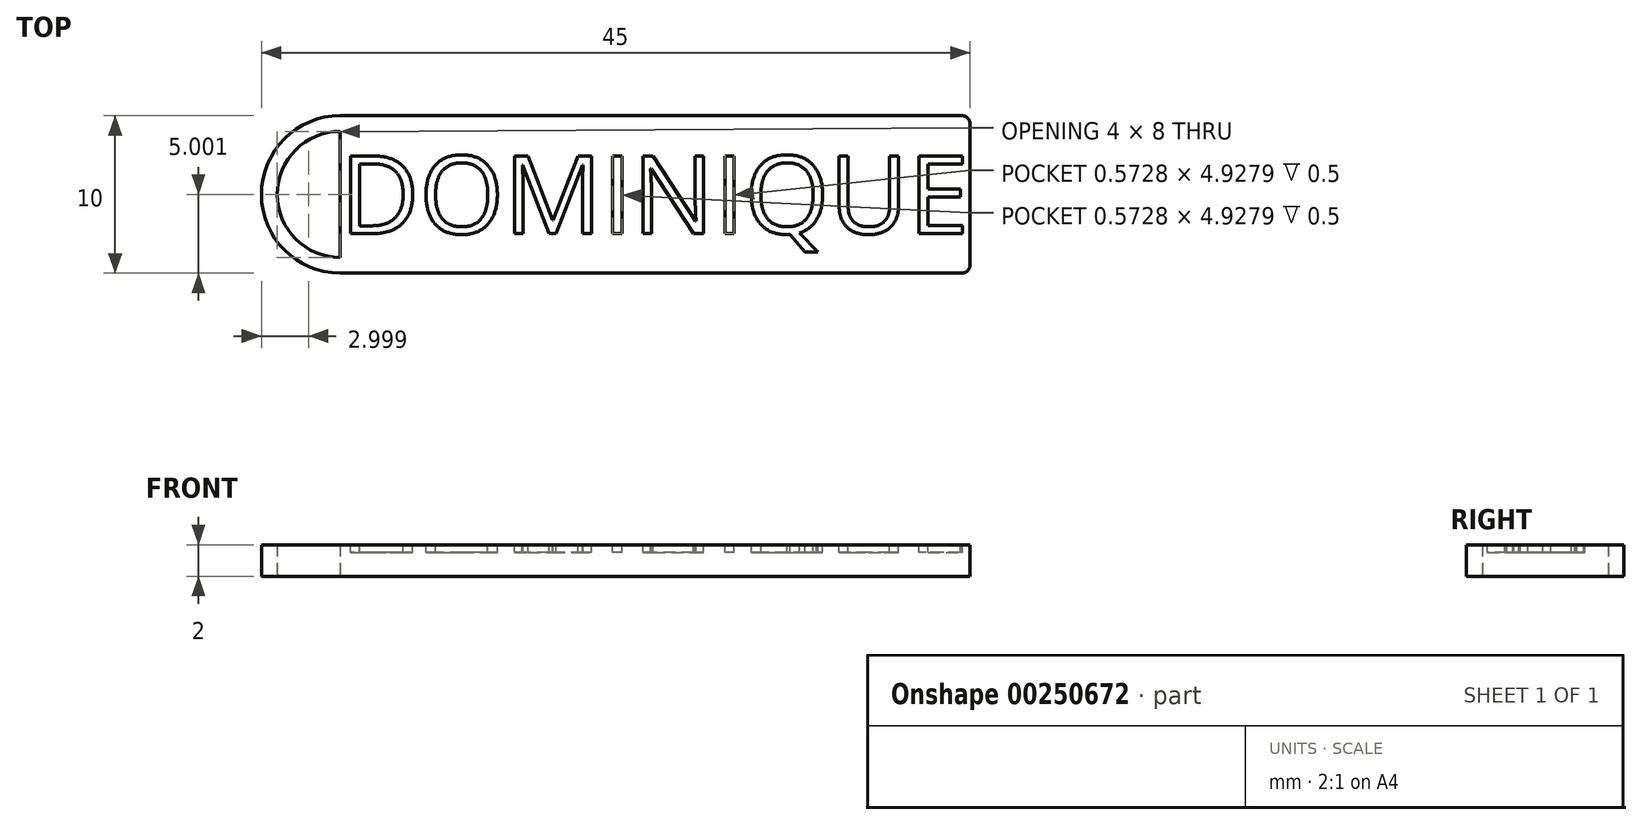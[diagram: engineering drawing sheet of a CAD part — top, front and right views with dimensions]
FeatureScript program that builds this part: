
annotation { "Feature Type Name" : "Feature", "Feature Type Description" : "" }
export const myFeature = defineFeature(function(context is Context, id is Id, definition is map)
    precondition{}
    {
        {
            var Q0;
            Q0=qCreatedBy(makeId("Top.planeOp"),FACE);
            var sketch = newSketch(context, id + "F0", { "sketchPlane" : qUnion([Q0])});
            skLineSegment(sketch, "E0.bottom", {"start": v(-5.27, 3.22) * mm, "end": v(34.73, 3.22) * mm});
            skLineSegment(sketch, "E0.top", {"start": v(-5.27, -6.78) * mm, "end": v(34.73, -6.78) * mm});
            skLineSegment(sketch, "E0.left", {"start": v(-5.27, 3.22) * mm, "end": v(-5.27, -6.78) * mm});
            skLineSegment(sketch, "E0.right", {"start": v(34.73, 3.22) * mm, "end": v(34.73, -6.78) * mm});
            skArc(sketch, "E1", {"start": v(-5.27, 3.22) * mm, "mid": v(-10.27, -1.78) * mm, "end": v(-5.27, -6.78) * mm});
            skArc(sketch, "E2", {"start": v(-5.27, 2.22) * mm, "mid": v(-9.27, -1.78) * mm, "end": v(-5.27, -5.78) * mm});
            skSolve(sketch);
        }
        {
            var Q0;
            Q0=qSketchRegion(id+"F0",true);
            extrude(context, id + "F4", {"entities" : qUnion([Q0]), "depth" : 2 * mm});
        }
        {
            var Q0;
            Q0=makeQuery(id+"F4.opExtrude","SWEPT_EDGE",EDGE,{"disambiguationData":[OSD([sQuery(id+"F0.wireOp",EDGE,"E0.top"),sQuery(id+"F0.wireOp",EDGE,"E0.right")])]});
            var Q1;
            Q1=makeQuery(id+"F4.opExtrude","SWEPT_EDGE",EDGE,{"disambiguationData":[OSD([sQuery(id+"F0.wireOp",EDGE,"E0.bottom"),sQuery(id+"F0.wireOp",EDGE,"E0.right")])]});
            fillet(context, id + "F1", {"entities" : qUnion([Q0, Q1]), "radius" : 0.5 * mm, "tangentPropagation" : true, "allowEdgeOverflow" : false});
        }
        {
            var Q0;
            Q0=makeQuery(id+"F4.opExtrude","CAP_FACE",FACE,{"disambiguationData":[OSD([sQuery(id+"F0.wireOp",EDGE,"E0.bottom"),sQuery(id+"F0.wireOp",EDGE,"E0.top"),sQuery(id+"F0.wireOp",EDGE,"E0.left"),sQuery(id+"F0.wireOp",EDGE,"E0.right"),sQuery(id+"F0.wireOp",EDGE,"E1"),sQuery(id+"F0.wireOp",EDGE,"E2")])],"isStart":false});
            var sketch = newSketch(context, id + "F2", { "sketchPlane" : qUnion([Q0])});
            skText(sketch, "E3", { "text": "DOMINIQUE", "fontName": "OpenSans-Regular.ttf"});
            skPoint(sketch, "E4", {"position": v(-5.27, -1.78) * mm});
            skPoint(sketch, "E5", {"position": v(34.73, -1.78) * mm});
            const initialGuessF2  = {"E3": [-0.00527, -0.00427, 1, 0, 0.00497]};
            skSetInitialGuess(sketch, initialGuessF2);
            skSolve(sketch);
        }
        {
            var Q0;
            Q0 = qSketchRegion(id + "F2", true);
            extrude(context, id + "F3", {"entities" : qUnion([Q0]), "operationType" : NewBodyOperationType.REMOVE, "oppositeDirection" : true, "depth" : 0.5 * mm});
        }
    });
